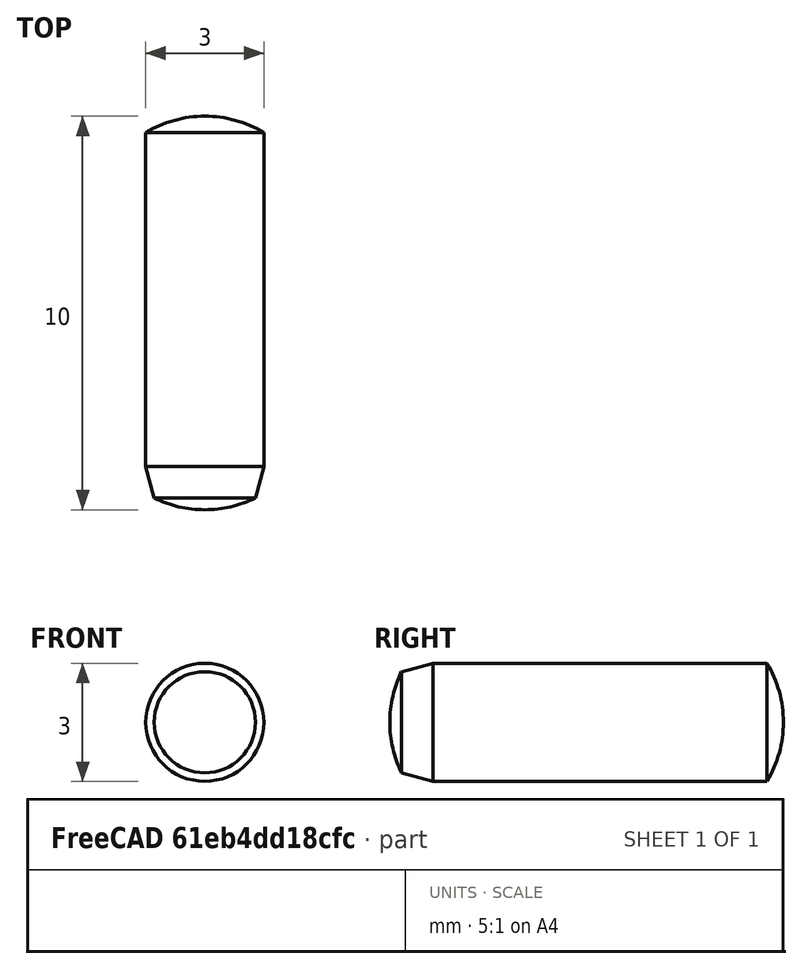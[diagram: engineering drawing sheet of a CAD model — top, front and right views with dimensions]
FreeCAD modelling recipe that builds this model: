
FCSTD DOCUMENT  (FreeCAD 0.15R4470 (Git))
Label: Zyl-Stift_DIN_6325-3x10
License: CC-BY 3.0
LicenseURL: http://creativecommons.org/licenses/by/3.0/
objects: Sketcher::SketchObject×1, PartDesign::Revolution×1
note: 3 computed .brp shape members not serialized (recipe doc carries the construction recipe); baked Part::Feature solids carry a one-line shape summary decoded from their .brp

FEATURE [Sketcher::SketchObject] Sketch
  Placement = pos=(0,0,0) rot=(0.57735,0.57735,0.57735;2.0944rad)
  sketch-geometry (5):
    g0: ArcOfCircle CenterX=2.60479 CenterY=0 CenterZ=0 NormalX=0 NormalY=0 NormalZ=1 Radius=2.90479 StartAngle=2.6831 EndAngle=3.14159
    g1: LineSegment StartX=0 StartY=1.28564 StartZ=0 EndX=0.8 EndY=1.5 EndZ=0
    g2: LineSegment StartX=0.8 StartY=1.5 StartZ=0 EndX=9.28274 EndY=1.5 EndZ=0
    g3: ArcOfCircle CenterX=6.79521 CenterY=0 CenterZ=0 NormalX=0 NormalY=0 NormalZ=1 Radius=2.90479 StartAngle=0 EndAngle=0.542629
    g4: LineSegment StartX=-0.3 StartY=0 StartZ=0 EndX=9.7 EndY=0 EndZ=0
  constraints (17):
    c: PointOnObject(g0,g-1)
    c: PointOnObject(g0,g-1)
    c: PointOnObject(g0,g-2)
    c: Coincident(g0,g1)
    c: Coincident(g1,g2)
    c: Horizontal(g2)
    c: PointOnObject(g3,g-1)
    c: Coincident(g3,g2)
    c: PointOnObject(g3,g-1)
    c: Coincident(g4,g0)
    c: Coincident(g4,g3)
    c: Equal(g0,g3)
    c: Angle(g4,g1) = 0.261799
    c: DistanceX(g4) = 10
    c: DistanceY(g-1,g1) = 1.5
    c: DistanceX(g1) = 0.8
    c: DistanceX(g0,g0) = 0.3
FEATURE [PartDesign::Revolution] Revolution  label="Zyl-Stift DIN 6325-3x10 #"
  Angle = 360
  Axis = (0,1,0)
  Base = (0,0,0)
  Placement = pos=(0,0,0) rot=(0.57735,0.57735,0.57735;2.0944rad)
  ReferenceAxis = -> Sketch [H_Axis]
  Sketch = -> Sketch
